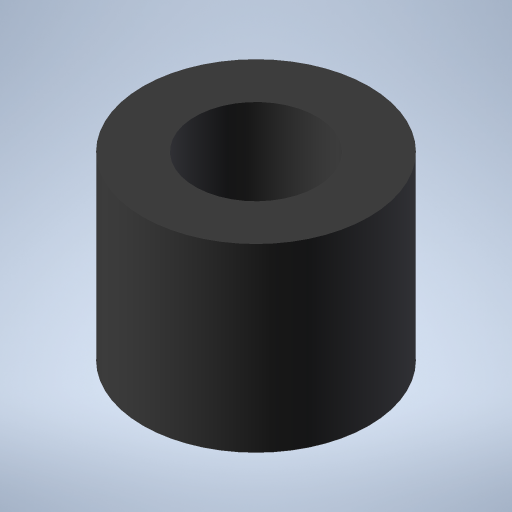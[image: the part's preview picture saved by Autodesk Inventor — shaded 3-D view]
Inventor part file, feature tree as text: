
AUTODESK INVENTOR PART (.ipt)
format: ipt  version: 2024.2 (Build 282272000, 272)  size: 203,264 bytes
history: native  units: in
note: dims shown in document units (in); Inventor stores cm internally (conversion verified against a paired STEP export)
features: extrude x1, sketch x1, other x1
ambient origin geometry x8: Origin, YZ Plane, XZ Plane, XY Plane, X Axis, Y Axis, Z Axis, Center Point
bodies: Solid1 (feature_tree)
feature tree (3):
  extrude  "Extrusion1"  TaperAngle=0.0deg  [1 undecoded]
  sketch  "Sketch1"  dims[d3=0.2126in d4=0.0in d5=0.0in]
  other  "Boss-Extrude1"
note: 1 required parameter value undecoded (feature->parameter linkage not recoverable at this tier; creation-order binding heuristic only, values carry confidence <= 0.55)
